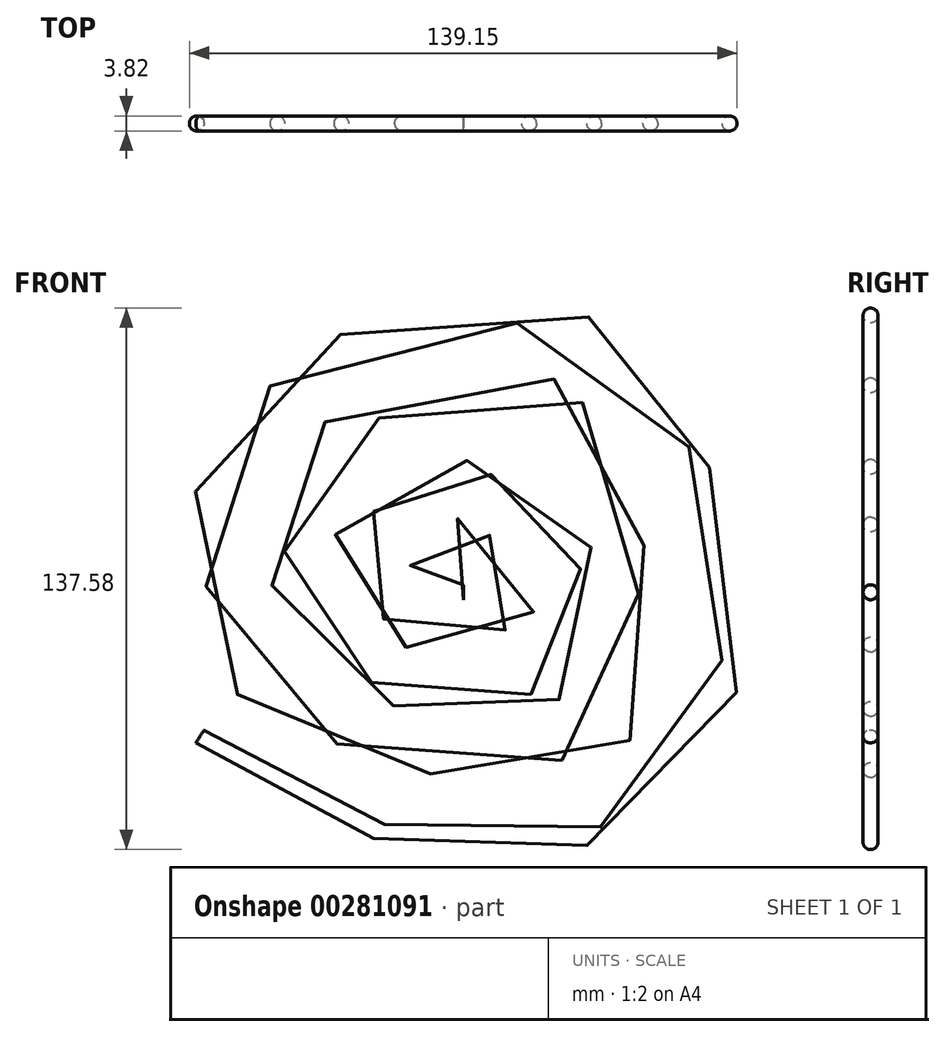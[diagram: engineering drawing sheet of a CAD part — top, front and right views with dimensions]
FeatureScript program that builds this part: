
annotation { "Feature Type Name" : "Feature", "Feature Type Description" : "" }
export const myFeature = defineFeature(function(context is Context, id is Id, definition is map)
    precondition{}
    {
        {
            var Q0;
            Q0=qCreatedBy(makeId("Front.planeOp"),FACE);
            var sketch = newSketch(context, id + "F0", { "sketchPlane" : qUnion([Q0])});
            skFitSpline(sketch, "E0", {"points": [v(0, 0) * mm, v(-15.59, 5.48) * mm, v(-3.65, 16.2) * mm, v(10.47, 14.5) * mm, v(16.56, 3.29) * mm, v(12.9, -10.1) * mm, v(0, -13.27) * mm, v(-17.3, -11.08) * mm, v(-25.82, -2.56) * mm, v(-30.93, 13.27) * mm, v(-23.14, 22.53) * mm, v(-4.14, 30.81) * mm, v(22.16, 28.37) * mm, v(30.2, 12.79) * mm, v(32.64, -14) * mm, v(23.63, -25.45) * mm, v(3.4, -29.6) * mm, v(-20.7, -25.94) * mm, v(-41.9, -11.57) * mm, v(-47.25, 12.79) * mm, v(-40.19, 36.9) * mm, v(-13.15, 48.1) * mm, v(32.4, 49.08) * mm, v(42.62, 19.36) * mm, v(47.5, -13.76) * mm, v(36.53, -40.55) * mm, v(2.44, -44.7) * mm, v(-34.1, -39.82) * mm, v(-61.86, -16.44) * mm, v(-67.22, 18.63) * mm, v(-53.1, 51.51) * mm, v(-7.3, 68.8) * mm, v(38, 65.64) * mm, v(57.24, 42.99) * mm, v(65.03, 4.02) * mm, v(64.79, -36.9) * mm, v(34.34, -61.74) * mm, v(-7.3, -61.5) * mm, v(-36.53, -57.85) * mm, v(-66.98, -36.66) * mm], "startDerivative": vector(-1120, 161.27) * mm, "endDerivative": vector(-996.14, 858.83) * mm});
            skSolve(sketch);
        }
        {
            var Q0;
            Q0=qCreatedBy(makeId("Right.planeOp"),FACE);
            var sketch = newSketch(context, id + "F1", { "sketchPlane" : qUnion([Q0])});
            skCircle(sketch, "E1", {"center": v(0, 0) * mm, "radius": 1.9 * mm});
            skSolve(sketch);
        }
        {
            var Q0;
            Q0=makeQuery(id+"F1.imprint","IMPRINT",FACE,{"disambiguationData":[TD([[makeQuery(id+"F1.imprint","IMPRINT",EDGE,{"derivedFrom":sQuery(id+"F1.wireOp",EDGE,"E1")}),1.0]])]});
            var Q1;
            Q1=sQuery(id+"F0.wireOp",EDGE,"E0");
            sweep(context, id + "F2", {"profiles" : qUnion([Q0]), "path" : qUnion([Q1])});
        }
    });
